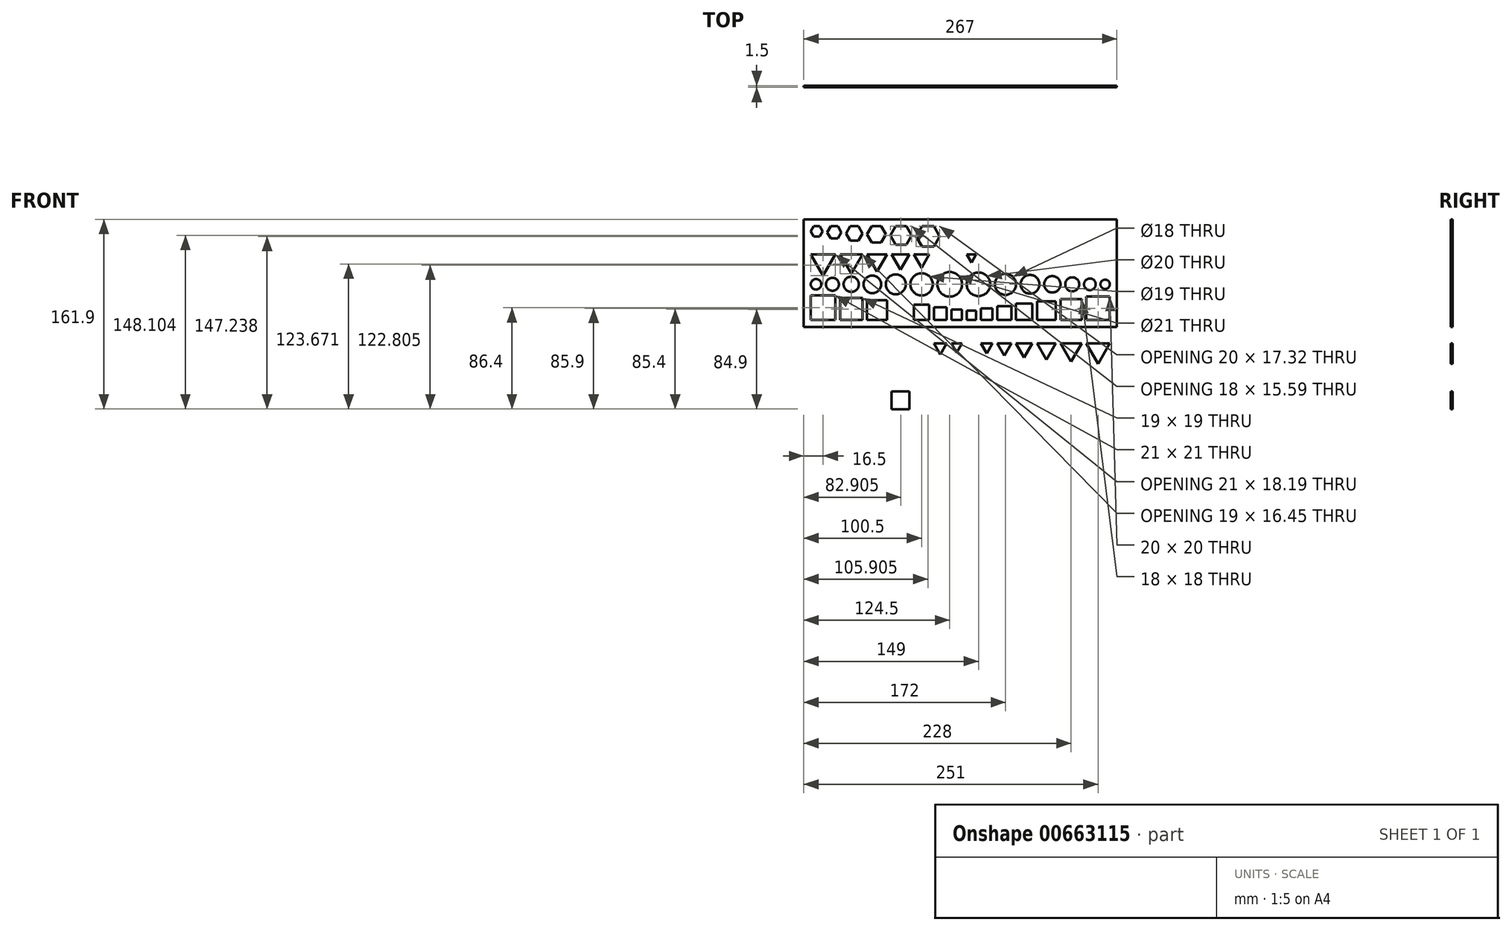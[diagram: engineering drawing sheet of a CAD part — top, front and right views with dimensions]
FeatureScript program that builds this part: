
annotation { "Feature Type Name" : "Feature", "Feature Type Description" : "" }
export const myFeature = defineFeature(function(context is Context, id is Id, definition is map)
    precondition{}
    {
        {
            var Q0;
            Q0=qCreatedBy(makeId("Front.planeOp"),FACE);
            var sketch = newSketch(context, id + "F0", { "sketchPlane" : qUnion([Q0])});
            skLineSegment(sketch, "E0.bottom", {"start": v(0, 0) * mm, "end": v(8, 0) * mm});
            skLineSegment(sketch, "E0.top", {"start": v(0, 8) * mm, "end": v(8, 8) * mm});
            skLineSegment(sketch, "E0.left", {"start": v(0, 0) * mm, "end": v(0, 8) * mm});
            skLineSegment(sketch, "E0.right", {"start": v(8, 0) * mm, "end": v(8, 8) * mm});
            skLineSegment(sketch, "E1.bottom", {"start": v(12, 0) * mm, "end": v(22, 0) * mm});
            skLineSegment(sketch, "E1.top", {"start": v(12, 10) * mm, "end": v(22, 10) * mm});
            skLineSegment(sketch, "E1.left", {"start": v(12, 0) * mm, "end": v(12, 10) * mm});
            skLineSegment(sketch, "E1.right", {"start": v(22, 0) * mm, "end": v(22, 10) * mm});
            skLineSegment(sketch, "E2.bottom", {"start": v(26, 0) * mm, "end": v(38, 0) * mm});
            skLineSegment(sketch, "E2.top", {"start": v(26, 12) * mm, "end": v(38, 12) * mm});
            skLineSegment(sketch, "E2.left", {"start": v(26, 0) * mm, "end": v(26, 12) * mm});
            skLineSegment(sketch, "E2.right", {"start": v(38, 0) * mm, "end": v(38, 12) * mm});
            skLineSegment(sketch, "E3.bottom", {"start": v(42, 0) * mm, "end": v(56, 0) * mm});
            skLineSegment(sketch, "E3.top", {"start": v(42, 14) * mm, "end": v(56, 14) * mm});
            skLineSegment(sketch, "E3.left", {"start": v(42, 0) * mm, "end": v(42, 14) * mm});
            skLineSegment(sketch, "E3.right", {"start": v(56, 0) * mm, "end": v(56, 14) * mm});
            skLineSegment(sketch, "E4.bottom", {"start": v(60, 0) * mm, "end": v(76, 0) * mm});
            skLineSegment(sketch, "E4.top", {"start": v(60, 16) * mm, "end": v(76, 16) * mm});
            skLineSegment(sketch, "E4.left", {"start": v(60, 0) * mm, "end": v(60, 16) * mm});
            skLineSegment(sketch, "E4.right", {"start": v(76, 0) * mm, "end": v(76, 16) * mm});
            skLineSegment(sketch, "E5.bottom", {"start": v(80, 0) * mm, "end": v(98, 0) * mm});
            skLineSegment(sketch, "E5.top", {"start": v(80, 18) * mm, "end": v(98, 18) * mm});
            skLineSegment(sketch, "E5.left", {"start": v(80, 0) * mm, "end": v(80, 18) * mm});
            skLineSegment(sketch, "E5.right", {"start": v(98, 0) * mm, "end": v(98, 18) * mm});
            skLineSegment(sketch, "E6.bottom", {"start": v(102, 0) * mm, "end": v(122, 0) * mm});
            skLineSegment(sketch, "E6.top", {"start": v(102, 20) * mm, "end": v(122, 20) * mm});
            skLineSegment(sketch, "E6.left", {"start": v(102, 0) * mm, "end": v(102, 20) * mm});
            skLineSegment(sketch, "E6.right", {"start": v(122, 0) * mm, "end": v(122, 20) * mm});
            skCircle(sketch, "E7", {"center": v(118, 30.5) * mm, "radius": 4 * mm});
            skCircle(sketch, "E8", {"center": v(105, 30.5) * mm, "radius": 5 * mm});
            skCircle(sketch, "E9", {"center": v(73, 30.5) * mm, "radius": 7 * mm});
            skCircle(sketch, "E10", {"center": v(90, 30.5) * mm, "radius": 6 * mm});
            skCircle(sketch, "E11", {"center": v(54, 30.5) * mm, "radius": 8 * mm});
            skCircle(sketch, "E12", {"center": v(33, 30.5) * mm, "radius": 9 * mm});
            skCircle(sketch, "E13", {"center": v(10, 30.5) * mm, "radius": 10 * mm});
            skLineSegment(sketch, "E14.bottom", {"start": v(-4, 0) * mm, "end": v(-13, 0) * mm});
            skLineSegment(sketch, "E14.top", {"start": v(-4, 9) * mm, "end": v(-13, 9) * mm});
            skLineSegment(sketch, "E14.left", {"start": v(-4, 0) * mm, "end": v(-4, 9) * mm});
            skLineSegment(sketch, "E14.right", {"start": v(-13, 0) * mm, "end": v(-13, 9) * mm});
            skLineSegment(sketch, "E15.bottom", {"start": v(-17, 0) * mm, "end": v(-28, 0) * mm});
            skLineSegment(sketch, "E15.top", {"start": v(-17, 11) * mm, "end": v(-28, 11) * mm});
            skLineSegment(sketch, "E15.left", {"start": v(-17, 0) * mm, "end": v(-17, 11) * mm});
            skLineSegment(sketch, "E15.right", {"start": v(-28, 0) * mm, "end": v(-28, 11) * mm});
            skLineSegment(sketch, "E16.bottom", {"start": v(-32, 0) * mm, "end": v(-45, 0) * mm});
            skLineSegment(sketch, "E16.top", {"start": v(-32, 13) * mm, "end": v(-45, 13) * mm});
            skLineSegment(sketch, "E16.left", {"start": v(-32, 0) * mm, "end": v(-32, 13) * mm});
            skLineSegment(sketch, "E16.right", {"start": v(-45, 0) * mm, "end": v(-45, 13) * mm});
            skLineSegment(sketch, "E17.bottom", {"start": v(-49, -75.9) * mm, "end": v(-64, -75.9) * mm});
            skLineSegment(sketch, "E17.top", {"start": v(-49, -60.9) * mm, "end": v(-64, -60.9) * mm});
            skLineSegment(sketch, "E17.left", {"start": v(-49, -75.9) * mm, "end": v(-49, -60.9) * mm});
            skLineSegment(sketch, "E17.right", {"start": v(-64, -75.9) * mm, "end": v(-64, -60.9) * mm});
            skLineSegment(sketch, "E18.bottom", {"start": v(-68, 0) * mm, "end": v(-85, 0) * mm});
            skLineSegment(sketch, "E18.top", {"start": v(-68, 17) * mm, "end": v(-85, 17) * mm});
            skLineSegment(sketch, "E18.left", {"start": v(-68, 0) * mm, "end": v(-68, 17) * mm});
            skLineSegment(sketch, "E18.right", {"start": v(-85, 0) * mm, "end": v(-85, 17) * mm});
            skLineSegment(sketch, "E19.bottom", {"start": v(-89, 0) * mm, "end": v(-108, 0) * mm});
            skLineSegment(sketch, "E19.top", {"start": v(-89, 19) * mm, "end": v(-108, 19) * mm});
            skLineSegment(sketch, "E19.left", {"start": v(-89, 0) * mm, "end": v(-89, 19) * mm});
            skLineSegment(sketch, "E19.right", {"start": v(-108, 0) * mm, "end": v(-108, 19) * mm});
            skLineSegment(sketch, "E20.bottom", {"start": v(-112, 0) * mm, "end": v(-133, 0) * mm});
            skLineSegment(sketch, "E20.top", {"start": v(-112, 21) * mm, "end": v(-133, 21) * mm});
            skLineSegment(sketch, "E20.left", {"start": v(-112, 0) * mm, "end": v(-112, 21) * mm});
            skLineSegment(sketch, "E20.right", {"start": v(-133, 0) * mm, "end": v(-133, 21) * mm});
            skCircle(sketch, "E21", {"center": v(-38.5, 30.5) * mm, "radius": 9.5 * mm});
            skCircle(sketch, "E22", {"center": v(-60.5, 30.5) * mm, "radius": 8.5 * mm});
            skCircle(sketch, "E23", {"center": v(-80.5, 30.5) * mm, "radius": 7.5 * mm});
            skCircle(sketch, "E24", {"center": v(-128.5, 30.5) * mm, "radius": 4.5 * mm});
            skCircle(sketch, "E25", {"center": v(-98.5, 30.5) * mm, "radius": 6.5 * mm});
            skCircle(sketch, "E26", {"center": v(-114.5, 30.5) * mm, "radius": 5.5 * mm});
            skCircle(sketch, "E27", {"center": v(-14.5, 30.5) * mm, "radius": 10.5 * mm});
            skCircle(sketch, "E28.cCircle", {"center": v(4, 53.69) * mm, "radius": 2.3 * mm, "construction": true});
            skLineSegment(sketch, "E28.0", {"start": v(0, 56) * mm, "end": v(8, 56) * mm});
            skLineSegment(sketch, "E28.1", {"start": v(8, 56) * mm, "end": v(4, 49.07) * mm});
            skLineSegment(sketch, "E28.2", {"start": v(4, 49.07) * mm, "end": v(0, 56) * mm});
            skPoint(sketch, "E28.0.midPoint", {"position": v(4, 56) * mm});
            skCircle(sketch, "E29.cCircle", {"center": v(17, -22.8) * mm, "radius": 2.89 * mm, "construction": true});
            skLineSegment(sketch, "E29.0", {"start": v(12, -19.9) * mm, "end": v(22, -19.9) * mm});
            skLineSegment(sketch, "E29.1", {"start": v(22, -19.9) * mm, "end": v(17, -28.57) * mm});
            skLineSegment(sketch, "E29.2", {"start": v(17, -28.57) * mm, "end": v(12, -19.9) * mm});
            skPoint(sketch, "E29.0.midPoint", {"position": v(17, -19.9) * mm});
            skCircle(sketch, "E30.cCircle", {"center": v(32, -23.37) * mm, "radius": 3.46 * mm, "construction": true});
            skLineSegment(sketch, "E30.0", {"start": v(26, -19.9) * mm, "end": v(38, -19.9) * mm});
            skLineSegment(sketch, "E30.1", {"start": v(38, -19.9) * mm, "end": v(32, -30.3) * mm});
            skLineSegment(sketch, "E30.2", {"start": v(32, -30.3) * mm, "end": v(26, -19.9) * mm});
            skPoint(sketch, "E30.0.midPoint", {"position": v(32, -19.9) * mm});
            skCircle(sketch, "E31.cCircle", {"center": v(49, -23.95) * mm, "radius": 4.04 * mm, "construction": true});
            skLineSegment(sketch, "E31.0", {"start": v(42, -19.9) * mm, "end": v(56, -19.9) * mm});
            skLineSegment(sketch, "E31.1", {"start": v(56, -19.9) * mm, "end": v(49, -32.03) * mm});
            skLineSegment(sketch, "E31.2", {"start": v(49, -32.03) * mm, "end": v(42, -19.9) * mm});
            skPoint(sketch, "E31.0.midPoint", {"position": v(49, -19.9) * mm});
            skCircle(sketch, "E32.cCircle", {"center": v(68, -24.53) * mm, "radius": 4.62 * mm, "construction": true});
            skLineSegment(sketch, "E32.0", {"start": v(60, -19.9) * mm, "end": v(76, -19.9) * mm});
            skLineSegment(sketch, "E32.1", {"start": v(76, -19.9) * mm, "end": v(68, -33.76) * mm});
            skLineSegment(sketch, "E32.2", {"start": v(68, -33.76) * mm, "end": v(60, -19.9) * mm});
            skPoint(sketch, "E32.0.midPoint", {"position": v(68, -19.9) * mm});
            skCircle(sketch, "E33.cCircle", {"center": v(89, -25.1) * mm, "radius": 5.2 * mm, "construction": true});
            skLineSegment(sketch, "E33.0", {"start": v(80, -19.9) * mm, "end": v(98, -19.9) * mm});
            skLineSegment(sketch, "E33.1", {"start": v(98, -19.9) * mm, "end": v(89, -35.5) * mm});
            skLineSegment(sketch, "E33.2", {"start": v(89, -35.5) * mm, "end": v(80, -19.9) * mm});
            skPoint(sketch, "E33.0.midPoint", {"position": v(89, -19.9) * mm});
            skCircle(sketch, "E34.cCircle", {"center": v(112, -25.68) * mm, "radius": 5.77 * mm, "construction": true});
            skLineSegment(sketch, "E34.0", {"start": v(102, -19.9) * mm, "end": v(122, -19.9) * mm});
            skLineSegment(sketch, "E34.1", {"start": v(122, -19.9) * mm, "end": v(112, -37.23) * mm});
            skLineSegment(sketch, "E34.2", {"start": v(112, -37.23) * mm, "end": v(102, -19.9) * mm});
            skPoint(sketch, "E34.0.midPoint", {"position": v(112, -19.9) * mm});
            skCircle(sketch, "E35.cCircle", {"center": v(-8.5, -22.5) * mm, "radius": 2.6 * mm, "construction": true});
            skLineSegment(sketch, "E35.0", {"start": v(-13, -19.9) * mm, "end": v(-4, -19.9) * mm});
            skLineSegment(sketch, "E35.1", {"start": v(-4, -19.9) * mm, "end": v(-8.5, -27.7) * mm});
            skLineSegment(sketch, "E35.2", {"start": v(-8.5, -27.7) * mm, "end": v(-13, -19.9) * mm});
            skPoint(sketch, "E35.0.midPoint", {"position": v(-8.5, -19.9) * mm});
            skCircle(sketch, "E36.cCircle", {"center": v(-22.5, -23.08) * mm, "radius": 3.18 * mm, "construction": true});
            skLineSegment(sketch, "E36.0", {"start": v(-28, -19.9) * mm, "end": v(-17, -19.9) * mm});
            skLineSegment(sketch, "E36.1", {"start": v(-17, -19.9) * mm, "end": v(-22.5, -29.43) * mm});
            skLineSegment(sketch, "E36.2", {"start": v(-22.5, -29.43) * mm, "end": v(-28, -19.9) * mm});
            skPoint(sketch, "E36.0.midPoint", {"position": v(-22.5, -19.9) * mm});
            skCircle(sketch, "E37.cCircle", {"center": v(-38.5, 52.25) * mm, "radius": 3.75 * mm, "construction": true});
            skLineSegment(sketch, "E37.0", {"start": v(-45, 56) * mm, "end": v(-32, 56) * mm});
            skLineSegment(sketch, "E37.1", {"start": v(-32, 56) * mm, "end": v(-38.5, 44.74) * mm});
            skLineSegment(sketch, "E37.2", {"start": v(-38.5, 44.74) * mm, "end": v(-45, 56) * mm});
            skPoint(sketch, "E37.0.midPoint", {"position": v(-38.5, 56) * mm});
            skCircle(sketch, "E38.cCircle", {"center": v(-56.5, 51.67) * mm, "radius": 4.33 * mm, "construction": true});
            skLineSegment(sketch, "E38.0", {"start": v(-64, 56) * mm, "end": v(-49, 56) * mm});
            skLineSegment(sketch, "E38.1", {"start": v(-49, 56) * mm, "end": v(-56.5, 43) * mm});
            skLineSegment(sketch, "E38.2", {"start": v(-56.5, 43) * mm, "end": v(-64, 56) * mm});
            skPoint(sketch, "E38.0.midPoint", {"position": v(-56.5, 56) * mm});
            skCircle(sketch, "E39.cCircle", {"center": v(-76.5, 51.1) * mm, "radius": 4.9 * mm, "construction": true});
            skLineSegment(sketch, "E39.0", {"start": v(-85, 56) * mm, "end": v(-68, 56) * mm});
            skLineSegment(sketch, "E39.1", {"start": v(-68, 56) * mm, "end": v(-76.5, 41.28) * mm});
            skLineSegment(sketch, "E39.2", {"start": v(-76.5, 41.28) * mm, "end": v(-85, 56) * mm});
            skPoint(sketch, "E39.0.midPoint", {"position": v(-76.5, 56) * mm});
            skCircle(sketch, "E40.cCircle", {"center": v(-98.5, 50.51) * mm, "radius": 5.48 * mm, "construction": true});
            skLineSegment(sketch, "E40.0", {"start": v(-108, 56) * mm, "end": v(-89, 56) * mm});
            skLineSegment(sketch, "E40.1", {"start": v(-89, 56) * mm, "end": v(-98.5, 39.54) * mm});
            skLineSegment(sketch, "E40.2", {"start": v(-98.5, 39.54) * mm, "end": v(-108, 56) * mm});
            skPoint(sketch, "E40.0.midPoint", {"position": v(-98.5, 56) * mm});
            skCircle(sketch, "E41.cCircle", {"center": v(-122.5, 49.94) * mm, "radius": 6.06 * mm, "construction": true});
            skLineSegment(sketch, "E41.0", {"start": v(-133, 56) * mm, "end": v(-112, 56) * mm});
            skLineSegment(sketch, "E41.1", {"start": v(-112, 56) * mm, "end": v(-122.5, 37.81) * mm});
            skLineSegment(sketch, "E41.2", {"start": v(-122.5, 37.81) * mm, "end": v(-133, 56) * mm});
            skPoint(sketch, "E41.0.midPoint", {"position": v(-122.5, 56) * mm});
            skLineSegment(sketch, "E42.bottom", {"start": v(-139, 86) * mm, "end": v(128, 86) * mm});
            skLineSegment(sketch, "E42.top", {"start": v(-139, -6) * mm, "end": v(128, -6) * mm});
            skLineSegment(sketch, "E42.left", {"start": v(-139, 86) * mm, "end": v(-139, -6) * mm});
            skLineSegment(sketch, "E42.right", {"start": v(128, 86) * mm, "end": v(128, -6) * mm});
            skLineSegment(sketch, "E43", {"start": v(-341.5, 80) * mm, "end": v(-25.9, 80) * mm});
            skCircle(sketch, "E44.cCircle", {"center": v(-128, 75.67) * mm, "radius": 4.33 * mm, "construction": true});
            skLineSegment(sketch, "E44.0", {"start": v(-130.5, 80) * mm, "end": v(-125.5, 80) * mm});
            skLineSegment(sketch, "E44.1", {"start": v(-125.5, 80) * mm, "end": v(-123, 75.67) * mm});
            skLineSegment(sketch, "E44.2", {"start": v(-123, 75.67) * mm, "end": v(-125.5, 71.34) * mm});
            skLineSegment(sketch, "E44.3", {"start": v(-125.5, 71.34) * mm, "end": v(-130.5, 71.34) * mm});
            skLineSegment(sketch, "E44.4", {"start": v(-130.5, 71.34) * mm, "end": v(-133, 75.67) * mm});
            skLineSegment(sketch, "E44.5", {"start": v(-133, 75.67) * mm, "end": v(-130.5, 80) * mm});
            skPoint(sketch, "E44.0.midPoint", {"position": v(-128, 80) * mm});
            skCircle(sketch, "E45.cCircle", {"center": v(-113, 74.8) * mm, "radius": 5.2 * mm, "construction": true});
            skLineSegment(sketch, "E45.0", {"start": v(-116, 80) * mm, "end": v(-110, 80) * mm});
            skLineSegment(sketch, "E45.1", {"start": v(-110, 80) * mm, "end": v(-107, 74.8) * mm});
            skLineSegment(sketch, "E45.2", {"start": v(-107, 74.8) * mm, "end": v(-110, 69.6) * mm});
            skLineSegment(sketch, "E45.3", {"start": v(-110, 69.6) * mm, "end": v(-116, 69.6) * mm});
            skLineSegment(sketch, "E45.4", {"start": v(-116, 69.6) * mm, "end": v(-119, 74.8) * mm});
            skLineSegment(sketch, "E45.5", {"start": v(-119, 74.8) * mm, "end": v(-116, 80) * mm});
            skPoint(sketch, "E45.0.midPoint", {"position": v(-113, 80) * mm});
            skCircle(sketch, "E46.cCircle", {"center": v(-96, 73.94) * mm, "radius": 6.06 * mm, "construction": true});
            skLineSegment(sketch, "E46.0", {"start": v(-99.5, 80) * mm, "end": v(-92.5, 80) * mm});
            skLineSegment(sketch, "E46.1", {"start": v(-92.5, 80) * mm, "end": v(-89, 73.94) * mm});
            skLineSegment(sketch, "E46.2", {"start": v(-89, 73.94) * mm, "end": v(-92.5, 67.87) * mm});
            skLineSegment(sketch, "E46.3", {"start": v(-92.5, 67.87) * mm, "end": v(-99.5, 67.87) * mm});
            skLineSegment(sketch, "E46.4", {"start": v(-99.5, 67.87) * mm, "end": v(-103, 73.94) * mm});
            skLineSegment(sketch, "E46.5", {"start": v(-103, 73.94) * mm, "end": v(-99.5, 80) * mm});
            skPoint(sketch, "E46.0.midPoint", {"position": v(-96, 80) * mm});
            skCircle(sketch, "E47.cCircle", {"center": v(-77, 73.07) * mm, "radius": 6.93 * mm, "construction": true});
            skLineSegment(sketch, "E47.0", {"start": v(-81, 80) * mm, "end": v(-73, 80) * mm});
            skLineSegment(sketch, "E47.1", {"start": v(-73, 80) * mm, "end": v(-69, 73.07) * mm});
            skLineSegment(sketch, "E47.2", {"start": v(-69, 73.07) * mm, "end": v(-73, 66.14) * mm});
            skLineSegment(sketch, "E47.3", {"start": v(-73, 66.14) * mm, "end": v(-81, 66.14) * mm});
            skLineSegment(sketch, "E47.4", {"start": v(-81, 66.14) * mm, "end": v(-85, 73.07) * mm});
            skLineSegment(sketch, "E47.5", {"start": v(-85, 73.07) * mm, "end": v(-81, 80) * mm});
            skPoint(sketch, "E47.0.midPoint", {"position": v(-77, 80) * mm});
            skCircle(sketch, "E48.cCircle", {"center": v(-56.1, 72.2) * mm, "radius": 7.8 * mm, "construction": true});
            skLineSegment(sketch, "E48.0", {"start": v(-60.6, 80) * mm, "end": v(-51.6, 80) * mm});
            skLineSegment(sketch, "E48.1", {"start": v(-51.6, 80) * mm, "end": v(-47.1, 72.2) * mm});
            skLineSegment(sketch, "E48.2", {"start": v(-47.1, 72.2) * mm, "end": v(-51.6, 64.4) * mm});
            skLineSegment(sketch, "E48.3", {"start": v(-51.6, 64.4) * mm, "end": v(-60.6, 64.4) * mm});
            skLineSegment(sketch, "E48.4", {"start": v(-60.6, 64.4) * mm, "end": v(-65.1, 72.2) * mm});
            skLineSegment(sketch, "E48.5", {"start": v(-65.1, 72.2) * mm, "end": v(-60.6, 80) * mm});
            skPoint(sketch, "E48.0.midPoint", {"position": v(-56.1, 80) * mm});
            skCircle(sketch, "E49.cCircle", {"center": v(-33.1, 71.34) * mm, "radius": 8.66 * mm, "construction": true});
            skLineSegment(sketch, "E49.0", {"start": v(-38.1, 80) * mm, "end": v(-28.1, 80) * mm});
            skLineSegment(sketch, "E49.1", {"start": v(-28.1, 80) * mm, "end": v(-23.1, 71.34) * mm});
            skLineSegment(sketch, "E49.2", {"start": v(-23.1, 71.34) * mm, "end": v(-28.1, 62.68) * mm});
            skLineSegment(sketch, "E49.3", {"start": v(-28.1, 62.68) * mm, "end": v(-38.1, 62.68) * mm});
            skLineSegment(sketch, "E49.4", {"start": v(-38.1, 62.68) * mm, "end": v(-43.1, 71.34) * mm});
            skLineSegment(sketch, "E49.5", {"start": v(-43.1, 71.34) * mm, "end": v(-38.1, 80) * mm});
            skPoint(sketch, "E49.0.midPoint", {"position": v(-33.1, 80) * mm});
            skSolve(sketch);
        }
        {
            var Q0;
            Q0=qSketchRegion(id+"F0",true);
            extrude(context, id + "F1", {"entities" : qUnion([Q0]), "depth" : 1.5 * mm, "offsetDistance" : 25 * mm});
        }
    });
